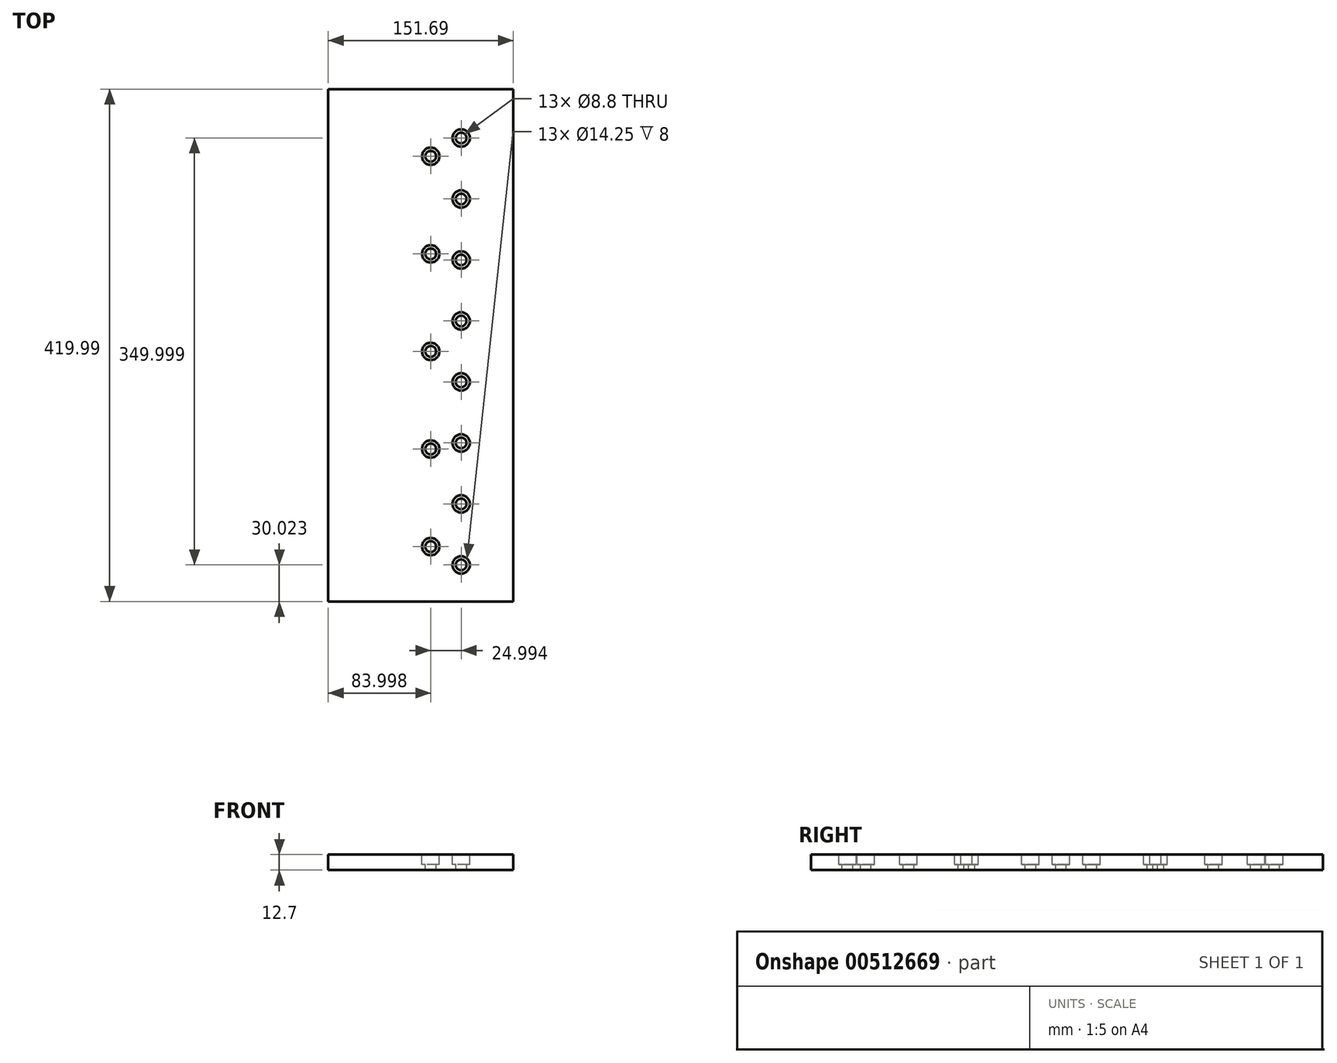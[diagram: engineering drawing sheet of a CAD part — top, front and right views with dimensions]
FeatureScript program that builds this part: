
annotation { "Feature Type Name" : "Feature", "Feature Type Description" : "" }
export const myFeature = defineFeature(function(context is Context, id is Id, definition is map)
    precondition{}
    {
        {
            var Q0;
            Q0=qCreatedBy(makeId("Top.planeOp"),FACE);
            var sketch = newSketch(context, id + "F0", { "sketchPlane" : qUnion([Q0])});
            skLineSegment(sketch, "E0.left", {"start": v(0, 0) * mm, "end": v(0, 100) * mm});
            skLineSegment(sketch, "E1.bottom", {"start": v(0, 100) * mm, "end": v(138.99, 100) * mm});
            skLineSegment(sketch, "E1.top", {"start": v(0, 519.99) * mm, "end": v(138.99, 519.99) * mm});
            skLineSegment(sketch, "E1.left", {"start": v(0, 100) * mm, "end": v(0, 519.99) * mm});
            skLineSegment(sketch, "E1.right", {"start": v(138.99, 100) * mm, "end": v(138.99, 519.99) * mm});
            skSolve(sketch);
        }
        {
            var Q0;
            Q0=makeQuery(id+"F0.imprint","IMPRINT",FACE,{"disambiguationData":[TD([[makeQuery(id+"F0.imprint","IMPRINT",EDGE,{"derivedFrom":sQuery(id+"F0.wireOp",EDGE,"E1.bottom")}),1.0]])]});
            var Q1;
            {var subQ0=sQuery(id+"F0.wireOp",EDGE,"d0de197a-86b7-45e0-b788-e49b3a4d63ff0.MirrorCS");Q1=makeQuery(id+"F0.imprint","IMPRINT",FACE,{"disambiguationData":[TD([[makeQuery(id+"F0.imprint","IMPRINT",EDGE,{"derivedFrom":subQ0}),1.0]])]});}
            var Q2;
            Q2=makeQuery(id+"F0.imprint","IMPRINT",FACE,{"disambiguationData":[TD([[makeQuery(id+"F0.imprint","IMPRINT",EDGE,{"derivedFrom":sQuery(id+"F0.wireOp",EDGE,"57696718-1a59-4942-ba76-f9a202f6e0f00.MirrorCS")}),-1.0]])]});
            var Q3;
            Q3=makeQuery(id+"F0.imprint","IMPRINT",FACE,{"disambiguationData":[TD([[makeQuery(id+"F0.imprint","IMPRINT",EDGE,{"derivedFrom":sQuery(id+"F0.wireOp",EDGE,"E0.bottom")}),1.0]])]});
            extrude(context, id + "F1", {"entities" : qUnion([Q0, Q1, Q2, Q3]), "depth" : 12.7 * mm, "offsetDistance" : 25.4 * mm});
        }
        {
            var Q0;
            Q0=makeQuery(id+"F1.opExtrude","CAP_FACE",FACE,{"disambiguationData":[OSD([sQuery(id+"F0.wireOp",EDGE,"E0.bottom"),sQuery(id+"F0.wireOp",EDGE,"E0.top"),sQuery(id+"F0.wireOp",EDGE,"E0.left"),sQuery(id+"F0.wireOp",EDGE,"E0.right"),sQuery(id+"F0.wireOp",EDGE,"E1.left"),sQuery(id+"F0.wireOp",EDGE,"E1.right"),sQuery(id+"F0.wireOp",EDGE,"080c81b6-708e-4d2e-9064-82ee56b91e7d0.MirrorCS"),sQuery(id+"F0.wireOp",EDGE,"738caccb-0e87-4d62-a264-7b76d52b53410.MirrorCS"),sQuery(id+"F0.wireOp",EDGE,"c537a215-8e43-4b40-a3bc-fe88c89c53900.MirrorCS"),sQuery(id+"F0.wireOp",EDGE,"d0de197a-86b7-45e0-b788-e49b3a4d63ff0.MirrorCS"),sQuery(id+"F0.wireOp",EDGE,"e2ebb85d-ef12-404e-bda6-a4c948c244480.MirrorCS"),sQuery(id+"F0.wireOp",EDGE,"4f822ed7-7937-4f70-b150-abadd6bdb38b0.MirrorCS")])],"isStart":false});
            var sketch = newSketch(context, id + "F2", { "sketchPlane" : qUnion([Q0])});
            skCircle(sketch, "E2.0.1.0", {"center": v(109, 130.02) * mm, "radius": 3.94 * mm});
            skLineSegment(sketch, "E3", {"start": v(109, 130.02) * mm, "end": v(84, 130.02) * mm});
            skLineSegment(sketch, "E4", {"start": v(84, 130.02) * mm, "end": v(84, 145.03) * mm});
            skCircle(sketch, "E5", {"center": v(84, 145.03) * mm, "radius": 3.94 * mm});
            skCircle(sketch, "E6.0.1.0", {"center": v(84, 225.03) * mm, "radius": 3.94 * mm});
            skCircle(sketch, "E6.0.2.0", {"center": v(84, 305.03) * mm, "radius": 3.94 * mm});
            skCircle(sketch, "E6.0.3.0", {"center": v(84, 385.03) * mm, "radius": 3.94 * mm});
            skCircle(sketch, "E6.0.4.0", {"center": v(84, 465.03) * mm, "radius": 3.94 * mm});
            skLineSegment(sketch, "E6.direction1", {"start": v(84, 145.03) * mm, "end": v(109.4, 145.03) * mm, "construction": true});
            skLineSegment(sketch, "E6.direction2", {"start": v(84, 145.03) * mm, "end": v(84, 225.03) * mm, "construction": true});
            skCircle(sketch, "E7.0.1.0", {"center": v(109, 180.02) * mm, "radius": 3.94 * mm});
            skCircle(sketch, "E7.0.2.0", {"center": v(109, 230.02) * mm, "radius": 3.94 * mm});
            skCircle(sketch, "E7.0.3.0", {"center": v(109, 280.02) * mm, "radius": 3.94 * mm});
            skCircle(sketch, "E7.0.4.0", {"center": v(109, 330.02) * mm, "radius": 3.94 * mm});
            skCircle(sketch, "E7.0.5.0", {"center": v(109, 380.02) * mm, "radius": 3.94 * mm});
            skCircle(sketch, "E7.0.6.0", {"center": v(109, 430.02) * mm, "radius": 3.94 * mm});
            skCircle(sketch, "E7.0.7.0", {"center": v(109, 480.02) * mm, "radius": 3.94 * mm});
            skLineSegment(sketch, "E7.direction1", {"start": v(109, 130.02) * mm, "end": v(134.4, 130.02) * mm, "construction": true});
            skLineSegment(sketch, "E7.direction2", {"start": v(109, 130.02) * mm, "end": v(109, 180.02) * mm, "construction": true});
            skSolve(sketch);
        }
        {
            var Q0;
            Q0=sQuery(id+"F2.wireOp",VERTEX,"369585ea-a5a8-48f9-a7d6-6d45eb4790a50.MirrorC.center");
            var Q1;
            Q1=sQuery(id+"F2.wireOp",VERTEX,"dc4692df-bbb7-4d35-9b86-f3c89d292bd40.MirrorC.center");
            var Q2;
            Q2=sQuery(id+"F2.wireOp",VERTEX,"827ec521-497c-415a-8a91-68c81789dce30.MirrorC.center");
            var Q3;
            Q3=sQuery(id+"F2.wireOp",VERTEX,"504b56b5-a912-4b94-964e-86b6e41d56610.MirrorC.center");
            var Q4;
            Q4=sQuery(id+"F2.wireOp",VERTEX,"08867103-cf83-4020-921b-704b2107b1880.MirrorC.center");
            var Q5;
            Q5=sQuery(id+"F2.wireOp",VERTEX,"f027c064-2164-4a1c-8134-cf0945e508530.MirrorC.center");
            var Q6;
            Q6=sQuery(id+"F2.wireOp",VERTEX,"1d53e6da-4eda-43f7-845c-ddebbddd65ab0.MirrorC.center");
            var Q7;
            Q7=sQuery(id+"F2.wireOp",VERTEX,"d9c16811-b7ed-4cf7-92b1-c218e3b24e9b0.MirrorC.center");
            var Q8;
            Q8=sQuery(id+"F2.wireOp",VERTEX,"4d1784d4-d9f1-4bf3-aa60-6d0eb5cfc9b30.MirrorC.center");
            var Q9;
            Q9=sQuery(id+"F2.wireOp",VERTEX,"c3d3d40f-c8d8-4817-ab36-241454a738970.MirrorC.center");
            var Q10;
            Q10=sQuery(id+"F2.wireOp",VERTEX,"00940fb4-4067-4279-8b7b-501bafbc080a0.MirrorC.center");
            var Q11;
            Q11=sQuery(id+"F2.wireOp",VERTEX,"35540bf8-e9be-4219-a35b-6c5fa5caef4e0.MirrorC.center");
            var Q12;
            Q12=sQuery(id+"F2.wireOp",VERTEX,"a2197021-0416-4242-940f-f3c927e397e70.MirrorC.center");
            var Q13;
            Q13=sQuery(id+"F2.wireOp",VERTEX,"3c1f7cd1-8bc0-464a-91ed-d8e7fa02f1e90.MirrorC.center");
            var Q14;
            Q14=sQuery(id+"F2.wireOp",VERTEX,"8d090ac3-828e-40c5-929c-1fd937b4586e0.MirrorC.center");
            var Q15;
            Q15=sQuery(id+"F2.wireOp",VERTEX,"833ffaa9-e007-467d-8a62-e57823d1d5400.MirrorC.center");
            var Q16;
            Q16=sQuery(id+"F2.wireOp",VERTEX,"ce068121-bfeb-46c0-b69f-9c2e4543a3e90.MirrorC.center");
            var Q17;
            Q17=sQuery(id+"F2.wireOp",VERTEX,"aa51e709-a912-4f8a-bc20-d9355a1062170.MirrorC.center");
            var Q18;
            Q18=sQuery(id+"F2.wireOp",VERTEX,"96e73aa2-773f-4aea-9a15-0a7106e0a5ee0.MirrorC.center");
            var Q19;
            Q19=sQuery(id+"F2.wireOp",VERTEX,"f8df947e-e0f6-4ce2-9d58-f6a0cbe6a5b50.MirrorC.center");
            var Q20;
            Q20=sQuery(id+"F2.wireOp",VERTEX,"683f6eda-570e-4446-8b53-f0f8cbc27b6c0.MirrorC.center");
            var Q21;
            Q21=sQuery(id+"F2.wireOp",VERTEX,"72cc6658-71ba-4e40-8768-41e9d242e7790.MirrorC.center");
            var Q22;
            Q22=sQuery(id+"F2.wireOp",VERTEX,"8aacdb62-c781-4cf9-b1b9-7ac2ee66a5f90.MirrorC.center");
            var Q23;
            Q23=sQuery(id+"F2.wireOp",VERTEX,"fbee1b28-1909-4ec2-a828-0418f95467090.MirrorC.center");
            var Q24;
            Q24=sQuery(id+"F2.wireOp",VERTEX,"ced36a8b-b441-4476-9a21-e1a5a7d9856b0.MirrorC.center");
            var Q25;
            Q25=sQuery(id+"F2.wireOp",VERTEX,"2081685d-42dc-47c4-95b8-52c1d426c0ff0.MirrorC.center");
            var Q26;
            Q26=sQuery(id+"F2.wireOp",VERTEX,"21ab06d6-2d3e-40b6-97b8-389702b345fe0.MirrorC.center");
            var Q27;
            Q27=sQuery(id+"F2.wireOp",VERTEX,"79d14713-f2ef-4459-b8f2-367e9ccdeb0f0.MirrorC.center");
            var Q28;
            Q28=sQuery(id+"F2.wireOp",VERTEX,"6b693a31-1740-4074-b8f5-e2b84b2727ec0.MirrorC.center");
            var Q29;
            Q29=sQuery(id+"F2.wireOp",VERTEX,"d0452018-95ae-44fe-aed6-f5443ceaa4d90.MirrorC.center");
            var Q30;
            Q30=sQuery(id+"F2.wireOp",VERTEX,"b10924f9-3357-47c8-9d26-83ea07b6218c0.MirrorC.center");
            var Q31;
            Q31=sQuery(id+"F2.wireOp",VERTEX,"fa7445c3-4edb-4c81-8016-e0e6fe2aafea0.MirrorC.center");
            var Q32;
            Q32=sQuery(id+"F2.wireOp",VERTEX,"9b13375c-b4e6-4446-8499-66ef3d748e3f0.MirrorC.center");
            var Q33;
            Q33=sQuery(id+"F2.wireOp",VERTEX,"12bc1277-524d-4e7e-913f-ba1b5aa30d9a0.MirrorC.center");
            var Q34;
            Q34=sQuery(id+"F2.wireOp",VERTEX,"ab084205-f0c4-49f2-bf57-be310257a5a90.MirrorC.center");
            var Q35;
            Q35=sQuery(id+"F2.wireOp",VERTEX,"ee0938a8-9660-41ef-994e-72495818419a0.MirrorC.center");
            var Q36;
            Q36=sQuery(id+"F2.wireOp",VERTEX,"467cb315-718e-4029-be8e-58d80902a2b00.MirrorC.center");
            var Q37;
            Q37=sQuery(id+"F2.wireOp",VERTEX,"dd2c6d8f-0712-44e8-930e-a445e61be8a60.MirrorC.center");
            var Q38;
            Q38=sQuery(id+"F2.wireOp",VERTEX,"c387b35a-df4f-4274-9531-2c6c86b64162.13.0.0.center");
            var Q39;
            Q39=sQuery(id+"F2.wireOp",VERTEX,"2e6e3978-d7f0-406f-a9cc-49524f8eebef.3.0.0.center");
            var Q40;
            Q40=sQuery(id+"F2.wireOp",VERTEX,"c387b35a-df4f-4274-9531-2c6c86b64162.12.0.0.center");
            var Q41;
            Q41=sQuery(id+"F2.wireOp",VERTEX,"c387b35a-df4f-4274-9531-2c6c86b64162.11.0.0.center");
            var Q42;
            Q42=sQuery(id+"F2.wireOp",VERTEX,"2e6e3978-d7f0-406f-a9cc-49524f8eebef.2.0.0.center");
            var Q43;
            Q43=sQuery(id+"F2.wireOp",VERTEX,"E6.0.4.0.center");
            var Q44;
            Q44=sQuery(id+"F2.wireOp",VERTEX,"E2.0.8.0.center");
            var Q45;
            Q45=sQuery(id+"F2.wireOp",VERTEX,"E2.0.7.0.center");
            var Q46;
            Q46=sQuery(id+"F2.wireOp",VERTEX,"E6.0.3.0.center");
            var Q47;
            Q47=sQuery(id+"F2.wireOp",VERTEX,"E2.0.6.0.center");
            var Q48;
            Q48=sQuery(id+"F2.wireOp",VERTEX,"E2.0.5.0.center");
            var Q49;
            Q49=sQuery(id+"F2.wireOp",VERTEX,"E6.0.2.0.center");
            var Q50;
            Q50=sQuery(id+"F2.wireOp",VERTEX,"E2.0.4.0.center");
            var Q51;
            Q51=sQuery(id+"F2.wireOp",VERTEX,"E6.direction2.end");
            var Q52;
            Q52=sQuery(id+"F2.wireOp",VERTEX,"E2.0.3.0.center");
            var Q53;
            Q53=sQuery(id+"F2.wireOp",VERTEX,"E2.0.2.0.center");
            var Q54;
            Q54=sQuery(id+"F2.wireOp",VERTEX,"E5.center");
            var Q55;
            Q55=sQuery(id+"F2.wireOp",VERTEX,"E3.start");
            var Q56;
            Q56=sQuery(id+"F2.wireOp",VERTEX,"E2.direction2.start");
            var Q57;
            Q57=sQuery(id+"F2.wireOp",VERTEX,"c387b35a-df4f-4274-9531-2c6c86b64162.direction1.start");
            var Q58;
            Q58=sQuery(id+"F2.wireOp",VERTEX,"4d4310a1-ca6d-4130-a819-48dea4285dc4.direction1.start");
            var Q59;
            Q59=sQuery(id+"F2.wireOp",VERTEX,"c387b35a-df4f-4274-9531-2c6c86b64162.direction1.end");
            var Q60;
            Q60=sQuery(id+"F2.wireOp",VERTEX,"4d4310a1-ca6d-4130-a819-48dea4285dc4.direction1.end");
            var Q61;
            Q61=sQuery(id+"F2.wireOp",VERTEX,"c387b35a-df4f-4274-9531-2c6c86b64162.2.0.0.center");
            var Q62;
            Q62=sQuery(id+"F2.wireOp",VERTEX,"c387b35a-df4f-4274-9531-2c6c86b64162.3.0.0.center");
            var Q63;
            Q63=sQuery(id+"F2.wireOp",VERTEX,"4d4310a1-ca6d-4130-a819-48dea4285dc4.2.0.0.center");
            var Q64;
            Q64=sQuery(id+"F2.wireOp",VERTEX,"c387b35a-df4f-4274-9531-2c6c86b64162.4.0.0.center");
            var Q65;
            Q65=sQuery(id+"F2.wireOp",VERTEX,"c387b35a-df4f-4274-9531-2c6c86b64162.5.0.0.center");
            var Q66;
            Q66=sQuery(id+"F2.wireOp",VERTEX,"c387b35a-df4f-4274-9531-2c6c86b64162.6.0.0.center");
            var Q67;
            Q67=sQuery(id+"F2.wireOp",VERTEX,"6MgekauG-bkbF-rjV7-3UdW-tPnbwlG1e7gO.start");
            var Q68;
            Q68=sQuery(id+"F2.wireOp",VERTEX,"c387b35a-df4f-4274-9531-2c6c86b64162.7.0.0.center");
            var Q69;
            Q69=sQuery(id+"F2.wireOp",VERTEX,"2e6e3978-d7f0-406f-a9cc-49524f8eebef.direction1.start");
            var Q70;
            Q70=sQuery(id+"F2.wireOp",VERTEX,"c387b35a-df4f-4274-9531-2c6c86b64162.8.0.0.center");
            var Q71;
            Q71=sQuery(id+"F2.wireOp",VERTEX,"c387b35a-df4f-4274-9531-2c6c86b64162.9.0.0.center");
            var Q72;
            Q72=sQuery(id+"F2.wireOp",VERTEX,"c387b35a-df4f-4274-9531-2c6c86b64162.10.0.0.center");
            var Q73;
            Q73=sQuery(id+"F2.wireOp",VERTEX,"2e6e3978-d7f0-406f-a9cc-49524f8eebef.direction1.end");
            var Q74;
            Q74=sQuery(id+"F2.wireOp",VERTEX,"E7.0.1.0.center");
            var Q75;
            Q75=sQuery(id+"F2.wireOp",VERTEX,"E7.0.2.0.center");
            var Q76;
            Q76=sQuery(id+"F2.wireOp",VERTEX,"E7.0.3.0.center");
            var Q77;
            Q77=sQuery(id+"F2.wireOp",VERTEX,"E7.0.4.0.center");
            var Q78;
            Q78=sQuery(id+"F2.wireOp",VERTEX,"E7.0.5.0.center");
            var Q79;
            Q79=sQuery(id+"F2.wireOp",VERTEX,"E7.0.6.0.center");
            var Q80;
            Q80=sQuery(id+"F2.wireOp",VERTEX,"E7.0.7.0.center");
            var Q81;
            Q81=makeQuery(id+"F1.opExtrude","SWEPT_BODY",BODY,{"disambiguationData":[OSD([sQuery(id+"F0.wireOp",EDGE,"E0.bottom"),sQuery(id+"F0.wireOp",EDGE,"E0.top"),sQuery(id+"F0.wireOp",EDGE,"E0.left"),sQuery(id+"F0.wireOp",EDGE,"E0.right"),sQuery(id+"F0.wireOp",EDGE,"E1.left"),sQuery(id+"F0.wireOp",EDGE,"E1.right"),sQuery(id+"F0.wireOp",EDGE,"080c81b6-708e-4d2e-9064-82ee56b91e7d0.MirrorCS"),sQuery(id+"F0.wireOp",EDGE,"738caccb-0e87-4d62-a264-7b76d52b53410.MirrorCS"),sQuery(id+"F0.wireOp",EDGE,"c537a215-8e43-4b40-a3bc-fe88c89c53900.MirrorCS"),sQuery(id+"F0.wireOp",EDGE,"d0de197a-86b7-45e0-b788-e49b3a4d63ff0.MirrorCS"),sQuery(id+"F0.wireOp",EDGE,"e2ebb85d-ef12-404e-bda6-a4c948c244480.MirrorCS"),sQuery(id+"F0.wireOp",EDGE,"4f822ed7-7937-4f70-b150-abadd6bdb38b0.MirrorCS")])]});
            hole(context, id + "F3", {"style" : HoleStyle.C_BORE, "endStyle" : HoleEndStyle.THROUGH, "standardTappedOrClearance" : lookupTablePath({ "standard" : "ISO", "fit" : "Normal", "size" : "M8", "type" : "Clearance" }), "standardBlindInLast" : lookupTablePath({ "fit" : "Standard", "standard" : "ISO", "size" : "M8", "type" : "Clearance" }), "holeDiameter" : 8.8 * mm, "cBoreDiameter" : 14.25 * mm, "cBoreDepth" : 8 * mm, "isTappedThrough" : true, "tappedDepth" : 12.7 * mm, "tapClearance" : 3, "locations" : qUnion([Q0, Q1, Q2, Q3, Q4, Q5, Q6, Q7, Q8, Q9, Q10, Q11, Q12, Q13, Q14, Q15, Q16, Q17, Q18, Q19, Q20, Q21, Q22, Q23, Q24, Q25, Q26, Q27, Q28, Q29, Q30, Q31, Q32, Q33, Q34, Q35, Q36, Q37, Q38, Q39, Q40, Q41, Q42, Q43, Q44, Q45, Q46, Q47, Q48, Q49, Q50, Q51, Q52, Q53, Q54, Q55, Q56, Q57, Q58, Q59, Q60, Q61, Q62, Q63, Q64, Q65, Q66, Q67, Q68, Q69, Q70, Q71, Q72, Q73, Q74, Q75, Q76, Q77, Q78, Q79, Q80]), "scope" : qUnion([Q81])});
        }
        {
            var Q0;
            Q0=makeQuery(id+"F1.opExtrude","SWEPT_FACE",FACE,{"disambiguationData":[OSD([sQuery(id+"F0.wireOp",EDGE,"E1.right")])]});
            var sketch = newSketch(context, id + "F4", { "sketchPlane" : qUnion([Q0])});
            skLineSegment(sketch, "E8.bottom", {"start": v(100, 12.7) * mm, "end": v(519.99, 12.7) * mm});
            skLineSegment(sketch, "E8.top", {"start": v(100, 0) * mm, "end": v(519.99, 0) * mm});
            skLineSegment(sketch, "E8.left", {"start": v(100, 12.7) * mm, "end": v(100, 0) * mm});
            skLineSegment(sketch, "E8.right", {"start": v(519.99, 12.7) * mm, "end": v(519.99, 0) * mm});
            skSolve(sketch);
        }
        {
            var Q0;
            Q0 = qSketchRegion(id + "F4", true);
            extrude(context, id + "F5", {"entities" : qUnion([Q0]), "operationType" : NewBodyOperationType.ADD, "depth" : 12.7 * mm, "offsetDistance" : 25.4 * mm});
        }
    });
